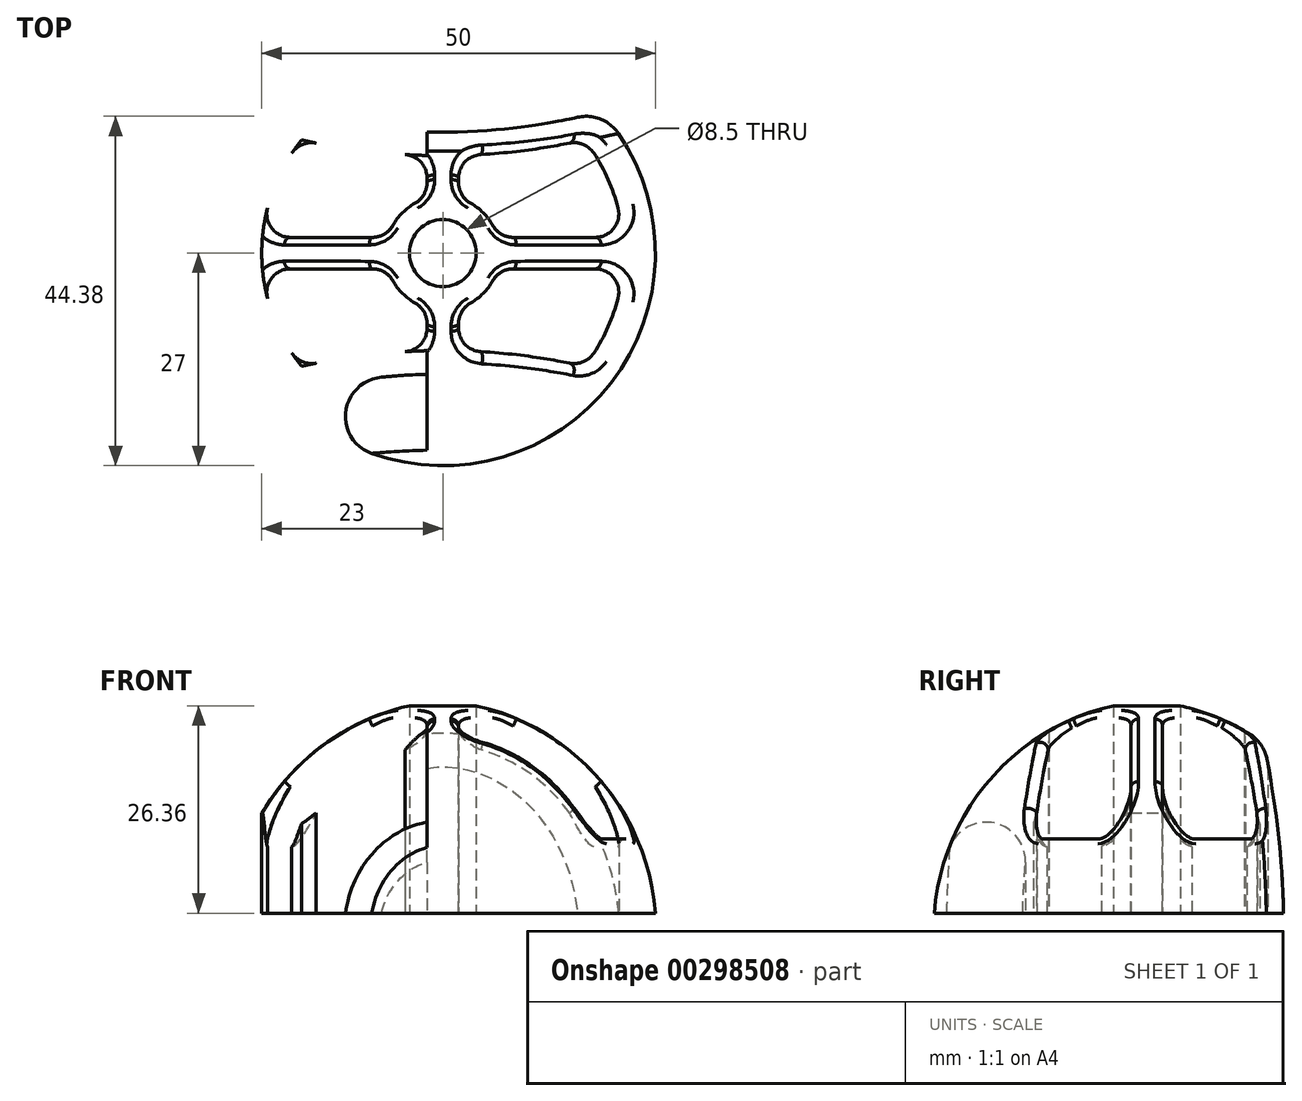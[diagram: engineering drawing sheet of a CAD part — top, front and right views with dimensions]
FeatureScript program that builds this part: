
annotation { "Feature Type Name" : "Feature", "Feature Type Description" : "" }
export const myFeature = defineFeature(function(context is Context, id is Id, definition is map)
    precondition{}
    {
        {
            var Q0;
            Q0=qCreatedBy(makeId("Top.planeOp"),FACE);
            var sketch = newSketch(context, id + "F0", { "sketchPlane" : qUnion([Q0])});
            skCircle(sketch, "E0", {"center": v(0, 0) * mm, "radius": 27 * mm});
            skSolve(sketch);
        }
        {
            var Q0;
            Q0=qCreatedBy(makeId("Right.planeOp"),FACE);
            var sketch = newSketch(context, id + "F1", { "sketchPlane" : qUnion([Q0])});
            skLineSegment(sketch, "E1", {"start": v(0, 0) * mm, "end": v(0, 27) * mm});
            skLineSegment(sketch, "E2", {"start": v(27, 0) * mm, "end": v(0, 0) * mm});
            skArc(sketch, "E3", {"start": v(27, 0) * mm, "mid": v(18.5, 18.5) * mm, "end": v(0, 27) * mm});
            skSolve(sketch);
        }
        {
            var Q0;
            Q0=makeQuery(id+"F1.imprint","IMPRINT",FACE,{"disambiguationData":[TD([[makeQuery(id+"F1.imprint","IMPRINT",EDGE,{"derivedFrom":sQuery(id+"F1.wireOp",EDGE,"E1")}),-1.0]])]});
            var Q1;
            Q1=sQuery(id+"F0.wireOp",EDGE,"E0");
            sweep(context, id + "F2", {"profiles" : qUnion([Q0]), "path" : qUnion([Q1])});
        }
        {
            var Q0;
            Q0=makeQuery(id+"F2.opSweep","SWEPT_FACE",FACE,{"disambiguationData":[OSD([sQuery(id+"F0.wireOp",EDGE,"E0"),sQuery(id+"F1.wireOp",EDGE,"E2")])]});
            var sketch = newSketch(context, id + "F3", { "sketchPlane" : qUnion([Q0])});
            skCircle(sketch, "E4", {"center": v(0, 0) * mm, "radius": 4.25 * mm});
            skArc(sketch, "E5.0", {"start": v(-17.95, -14.38) * mm, "mid": v(-23, 0) * mm, "end": v(-17.95, 14.38) * mm});
            skCircle(sketch, "E6.0", {"center": v(0, 0) * mm, "radius": 7.25 * mm});
            skLineSegment(sketch, "E7", {"start": v(0, 0) * mm, "end": v(-30.25, 0) * mm, "construction": true});
            skLineSegment(sketch, "E8", {"start": v(-6.97, -2) * mm, "end": v(-22.91, -2) * mm});
            skLineSegment(sketch, "E9", {"start": v(-6.97, 2) * mm, "end": v(-22.91, 2) * mm});
            skLineSegment(sketch, "E10.1.0", {"start": v(2, -6.97) * mm, "end": v(2, -15.4) * mm});
            skLineSegment(sketch, "E10.1.1", {"start": v(-2, -6.97) * mm, "end": v(-2, -15.4) * mm});
            skLineSegment(sketch, "E10.2.0", {"start": v(6.97, 2) * mm, "end": v(22.91, 2) * mm});
            skLineSegment(sketch, "E10.2.1", {"start": v(6.97, -2) * mm, "end": v(22.91, -2) * mm});
            skLineSegment(sketch, "E10.3.0", {"start": v(-2, 6.97) * mm, "end": v(-2, 15.4) * mm});
            skLineSegment(sketch, "E10.3.1", {"start": v(2, 6.97) * mm, "end": v(2, 15.4) * mm});
            skCircle(sketch, "E11.0", {"center": v(0, 0) * mm, "radius": 27 * mm});
            skArc(sketch, "E12", {"start": v(20.12, -18) * mm, "mid": v(0, -15.37) * mm, "end": v(-20.12, -18) * mm});
            skArc(sketch, "E13.MirrorCS", {"start": v(20.12, 18) * mm, "mid": v(0, 15.37) * mm, "end": v(-20.12, 18) * mm});
            skLineSegment(sketch, "E14", {"start": v(-20.12, -18) * mm, "end": v(20.12, -18) * mm, "construction": true});
            skArc(sketch, "E15.0", {"start": v(17.95, -14.38) * mm, "mid": v(0, -12.37) * mm, "end": v(-17.95, -14.38) * mm});
            skArc(sketch, "E16.MirrorCS", {"start": v(17.95, 14.38) * mm, "mid": v(0, 12.37) * mm, "end": v(-17.95, 14.38) * mm});
            skArc(sketch, "E17.trimOffspring", {"start": v(17.95, 14.38) * mm, "mid": v(23, 0) * mm, "end": v(17.95, -14.38) * mm});
            skPoint(sketch, "E18.orphan", {"position": v(-22.15, 15.44) * mm});
            skPoint(sketch, "E19.orphan", {"position": v(-22.15, -15.44) * mm});
            skPoint(sketch, "E20.orphan", {"position": v(22.15, -15.44) * mm});
            skPoint(sketch, "E21.orphan", {"position": v(22.15, 15.44) * mm});
            skLineSegment(sketch, "E22", {"start": v(-20.12, 18) * mm, "end": v(20.12, 18) * mm, "construction": true});
            skSolve(sketch);
        }
        {
            var Q0;
            {var subQ0=sQuery(id+"F3.wireOp",EDGE,"E8");Q0=makeQuery(id+"F3.imprint","IMPRINT",FACE,{"disambiguationData":[TD([[makeQuery(id+"F3.imprint","IMPRINT",EDGE,{"derivedFrom":subQ0}),1.0]])]});}
            var Q1;
            {var subQ0=sQuery(id+"F3.wireOp",EDGE,"E9");Q1=makeQuery(id+"F3.imprint","IMPRINT",FACE,{"disambiguationData":[TD([[makeQuery(id+"F3.imprint","IMPRINT",EDGE,{"derivedFrom":subQ0}),-1.0]])]});}
            var Q2;
            {var subQ0=sQuery(id+"F3.wireOp",EDGE,"E10.2.0");Q2=makeQuery(id+"F3.imprint","IMPRINT",FACE,{"disambiguationData":[TD([[makeQuery(id+"F3.imprint","IMPRINT",EDGE,{"derivedFrom":subQ0}),1.0]])]});}
            var Q3;
            {var subQ0=sQuery(id+"F3.wireOp",EDGE,"E10.1.0");Q3=makeQuery(id+"F3.imprint","IMPRINT",FACE,{"disambiguationData":[TD([[makeQuery(id+"F3.imprint","IMPRINT",EDGE,{"derivedFrom":subQ0}),1.0]])]});}
            var Q4;
            Q4=makeQuery(id+"F3.imprint","IMPRINT",FACE,{"disambiguationData":[TD([[makeQuery(id+"F3.imprint","IMPRINT",EDGE,{"derivedFrom":sQuery(id+"F3.wireOp",EDGE,"E4")}),1.0]])]});
            extrude(context, id + "F4", {"entities" : qUnion([Q0, Q1, Q2, Q3, Q4]), "operationType" : NewBodyOperationType.REMOVE, "endBound" : BoundingType.THROUGH_ALL, "oppositeDirection" : true, "depth" : 25 * mm});
        }
        {
            var Q0;
            Q0=makeQuery(id+"F4.boolean.opBoolean","COPY",EDGE,{"derivedFrom":makeQuery(id+"F4.opExtrude","SWEPT_EDGE",EDGE,{"disambiguationData":[OSD([sQuery(id+"F3.wireOp",EDGE,"E6.0"),sQuery(id+"F3.wireOp",EDGE,"E10.1.1")])]})});
            var Q1;
            Q1=makeQuery(id+"F4.boolean.opBoolean","COPY",EDGE,{"derivedFrom":makeQuery(id+"F4.opExtrude","SWEPT_EDGE",EDGE,{"disambiguationData":[OSD([sQuery(id+"F3.wireOp",EDGE,"E6.0"),sQuery(id+"F3.wireOp",EDGE,"E8")])]})});
            var Q2;
            Q2=makeQuery(id+"F4.boolean.opBoolean","COPY",EDGE,{"derivedFrom":makeQuery(id+"F4.opExtrude","SWEPT_EDGE",EDGE,{"disambiguationData":[OSD([sQuery(id+"F3.wireOp",EDGE,"E6.0"),sQuery(id+"F3.wireOp",EDGE,"E10.3.0")])]})});
            var Q3;
            Q3=makeQuery(id+"F4.boolean.opBoolean","COPY",EDGE,{"derivedFrom":makeQuery(id+"F4.opExtrude","SWEPT_EDGE",EDGE,{"disambiguationData":[OSD([sQuery(id+"F3.wireOp",EDGE,"E6.0"),sQuery(id+"F3.wireOp",EDGE,"E9")])]})});
            var Q4;
            Q4=makeQuery(id+"F4.boolean.opBoolean","COPY",EDGE,{"derivedFrom":makeQuery(id+"F4.opExtrude","SWEPT_EDGE",EDGE,{"disambiguationData":[OSD([sQuery(id+"F3.wireOp",EDGE,"E6.0"),sQuery(id+"F3.wireOp",EDGE,"E10.3.1")])]})});
            var Q5;
            Q5=makeQuery(id+"F4.boolean.opBoolean","COPY",EDGE,{"derivedFrom":makeQuery(id+"F4.opExtrude","SWEPT_EDGE",EDGE,{"disambiguationData":[OSD([sQuery(id+"F3.wireOp",EDGE,"E6.0"),sQuery(id+"F3.wireOp",EDGE,"E10.2.0")])]})});
            var Q6;
            Q6=makeQuery(id+"F4.boolean.opBoolean","COPY",EDGE,{"derivedFrom":makeQuery(id+"F4.opExtrude","SWEPT_EDGE",EDGE,{"disambiguationData":[OSD([sQuery(id+"F3.wireOp",EDGE,"E6.0"),sQuery(id+"F3.wireOp",EDGE,"E10.2.1")])]})});
            var Q7;
            Q7=makeQuery(id+"F4.boolean.opBoolean","COPY",EDGE,{"derivedFrom":makeQuery(id+"F4.opExtrude","SWEPT_EDGE",EDGE,{"disambiguationData":[OSD([sQuery(id+"F3.wireOp",EDGE,"E6.0"),sQuery(id+"F3.wireOp",EDGE,"E10.1.0")])]})});
            var Q8;
            Q8=makeQuery(id+"F4.boolean.opBoolean","COPY",EDGE,{"derivedFrom":makeQuery(id+"F4.opExtrude","SWEPT_EDGE",EDGE,{"disambiguationData":[OSD([sQuery(id+"F3.wireOp",EDGE,"E5.0"),sQuery(id+"F3.wireOp",EDGE,"E10.1.1")])]})});
            var Q9;
            Q9=makeQuery(id+"F4.boolean.opBoolean","COPY",EDGE,{"derivedFrom":makeQuery(id+"F4.opExtrude","SWEPT_EDGE",EDGE,{"disambiguationData":[OSD([sQuery(id+"F3.wireOp",EDGE,"E5.0"),sQuery(id+"F3.wireOp",EDGE,"E8")])]})});
            var Q10;
            Q10=makeQuery(id+"F4.boolean.opBoolean","COPY",EDGE,{"derivedFrom":makeQuery(id+"F4.opExtrude","SWEPT_EDGE",EDGE,{"disambiguationData":[OSD([sQuery(id+"F3.wireOp",EDGE,"E5.0"),sQuery(id+"F3.wireOp",EDGE,"E9")])]})});
            var Q11;
            Q11=makeQuery(id+"F4.boolean.opBoolean","COPY",EDGE,{"derivedFrom":makeQuery(id+"F4.opExtrude","SWEPT_EDGE",EDGE,{"disambiguationData":[OSD([sQuery(id+"F3.wireOp",EDGE,"E5.0"),sQuery(id+"F3.wireOp",EDGE,"E10.3.0")])]})});
            var Q12;
            Q12=makeQuery(id+"F4.boolean.opBoolean","COPY",EDGE,{"derivedFrom":makeQuery(id+"F4.opExtrude","SWEPT_EDGE",EDGE,{"disambiguationData":[OSD([sQuery(id+"F3.wireOp",EDGE,"E5.0"),sQuery(id+"F3.wireOp",EDGE,"E10.3.1")])]})});
            var Q13;
            Q13=makeQuery(id+"F4.boolean.opBoolean","COPY",EDGE,{"derivedFrom":makeQuery(id+"F4.opExtrude","SWEPT_EDGE",EDGE,{"disambiguationData":[OSD([sQuery(id+"F3.wireOp",EDGE,"E5.0"),sQuery(id+"F3.wireOp",EDGE,"E10.2.0")])]})});
            var Q14;
            Q14=makeQuery(id+"F4.boolean.opBoolean","COPY",EDGE,{"derivedFrom":makeQuery(id+"F4.opExtrude","SWEPT_EDGE",EDGE,{"disambiguationData":[OSD([sQuery(id+"F3.wireOp",EDGE,"E5.0"),sQuery(id+"F3.wireOp",EDGE,"E10.2.1")])]})});
            var Q15;
            Q15=makeQuery(id+"F4.boolean.opBoolean","COPY",EDGE,{"derivedFrom":makeQuery(id+"F4.opExtrude","SWEPT_EDGE",EDGE,{"disambiguationData":[OSD([sQuery(id+"F3.wireOp",EDGE,"E5.0"),sQuery(id+"F3.wireOp",EDGE,"E10.1.0")])]})});
            var Q16;
            Q16=makeQuery(id+"F4.boolean.opBoolean","COPY",EDGE,{"derivedFrom":makeQuery(id+"F4.opExtrude","SWEPT_EDGE",EDGE,{"disambiguationData":[OSD([sQuery(id+"F3.wireOp",EDGE,"E16.MirrorCS"),sQuery(id+"F3.wireOp",EDGE,"E17.trimOffspring")])]})});
            var Q17;
            Q17=makeQuery(id+"F4.boolean.opBoolean","COPY",EDGE,{"derivedFrom":makeQuery(id+"F4.opExtrude","SWEPT_EDGE",EDGE,{"disambiguationData":[OSD([sQuery(id+"F3.wireOp",EDGE,"E15.0"),sQuery(id+"F3.wireOp",EDGE,"E17.trimOffspring")])]})});
            fillet(context, id + "F5", {"entities" : qUnion([Q0, Q1, Q2, Q3, Q4, Q5, Q6, Q7, Q8, Q9, Q10, Q11, Q12, Q13, Q14, Q15, Q16, Q17]), "radius" : 3 * mm, "tangentPropagation" : true, "allowEdgeOverflow" : false});
        }
        {
            var Q0;
            Q0=makeQuery(id+"F5.opFillet","BLEND_EDGE",EDGE,{"blendedFrom":[makeQuery(id+"F4.boolean.opBoolean","COPY",EDGE,{"derivedFrom":makeQuery(id+"F4.opExtrude","SWEPT_EDGE",EDGE,{"disambiguationData":[OSD([sQuery(id+"F3.wireOp",EDGE,"E6.0"),sQuery(id+"F3.wireOp",EDGE,"E10.3.1")])]})}),makeQuery(id+"F2.opSweep","SWEPT_FACE",FACE,{"disambiguationData":[OSD([sQuery(id+"F0.wireOp",EDGE,"E0"),sQuery(id+"F1.wireOp",EDGE,"E3")])]})],"blendedInto":[makeQuery(id+"F2.opSweep","SWEPT_FACE",FACE,{"disambiguationData":[OSD([sQuery(id+"F0.wireOp",EDGE,"E0"),sQuery(id+"F1.wireOp",EDGE,"E3")])]})]});
            var Q1;
            Q1=makeQuery(id+"F5.opFillet","BLEND_EDGE",EDGE,{"blendedFrom":[makeQuery(id+"F4.boolean.opBoolean","COPY",EDGE,{"derivedFrom":makeQuery(id+"F4.opExtrude","SWEPT_EDGE",EDGE,{"disambiguationData":[OSD([sQuery(id+"F3.wireOp",EDGE,"E6.0"),sQuery(id+"F3.wireOp",EDGE,"E10.1.1")])]})}),makeQuery(id+"F2.opSweep","SWEPT_FACE",FACE,{"disambiguationData":[OSD([sQuery(id+"F0.wireOp",EDGE,"E0"),sQuery(id+"F1.wireOp",EDGE,"E3")])]})],"blendedInto":[makeQuery(id+"F2.opSweep","SWEPT_FACE",FACE,{"disambiguationData":[OSD([sQuery(id+"F0.wireOp",EDGE,"E0"),sQuery(id+"F1.wireOp",EDGE,"E3")])]})]});
            var Q2;
            Q2=makeQuery(id+"F5.opFillet","BLEND_EDGE",EDGE,{"blendedFrom":[makeQuery(id+"F4.boolean.opBoolean","COPY",EDGE,{"derivedFrom":makeQuery(id+"F4.opExtrude","SWEPT_EDGE",EDGE,{"disambiguationData":[OSD([sQuery(id+"F3.wireOp",EDGE,"E6.0"),sQuery(id+"F3.wireOp",EDGE,"E10.3.0")])]})}),makeQuery(id+"F2.opSweep","SWEPT_FACE",FACE,{"disambiguationData":[OSD([sQuery(id+"F0.wireOp",EDGE,"E0"),sQuery(id+"F1.wireOp",EDGE,"E3")])]})],"blendedInto":[makeQuery(id+"F2.opSweep","SWEPT_FACE",FACE,{"disambiguationData":[OSD([sQuery(id+"F0.wireOp",EDGE,"E0"),sQuery(id+"F1.wireOp",EDGE,"E3")])]})]});
            var Q3;
            Q3=makeQuery(id+"F5.opFillet","BLEND_EDGE",EDGE,{"blendedFrom":[makeQuery(id+"F4.boolean.opBoolean","COPY",EDGE,{"derivedFrom":makeQuery(id+"F4.opExtrude","SWEPT_EDGE",EDGE,{"disambiguationData":[OSD([sQuery(id+"F3.wireOp",EDGE,"E6.0"),sQuery(id+"F3.wireOp",EDGE,"E10.2.1")])]})}),makeQuery(id+"F2.opSweep","SWEPT_FACE",FACE,{"disambiguationData":[OSD([sQuery(id+"F0.wireOp",EDGE,"E0"),sQuery(id+"F1.wireOp",EDGE,"E3")])]})],"blendedInto":[makeQuery(id+"F2.opSweep","SWEPT_FACE",FACE,{"disambiguationData":[OSD([sQuery(id+"F0.wireOp",EDGE,"E0"),sQuery(id+"F1.wireOp",EDGE,"E3")])]})]});
            var Q4;
            Q4=makeQuery(id+"F4.boolean.opBoolean","COPY",EDGE,{"derivedFrom":makeQuery(id+"F4.opExtrude","CAP_EDGE",EDGE,{"disambiguationData":[OSD([sQuery(id+"F3.wireOp",EDGE,"E4")])],"isStart":true})});
            fillet(context, id + "F6", {"entities" : qUnion([Q0, Q1, Q2, Q3, Q4]), "radius" : 1 * mm, "tangentPropagation" : true, "allowEdgeOverflow" : false});
        }
        {
            var Q0;
            {var subQ0=sQuery(id+"F3.wireOp",EDGE,"E12");var subQ1=sQuery(id+"F3.wireOp",EDGE,"E11.0");var subQ2=makeQuery(id+"F3.imprint","INTERSECT",VERTEX,{"disambiguationData":[OD(0.0)],"derivedFrom":[subQ1,subQ0]});Q0=makeQuery(id+"F3.imprint","IMPRINT",FACE,{"disambiguationData":[TD([[makeQuery(id+"F3.imprint","IMPRINT",EDGE,{"disambiguationData":[TD([[subQ2,-1.0]])],"derivedFrom":subQ1}),-1.0]])]});}
            var Q1;
            {var subQ0=sQuery(id+"F3.wireOp",EDGE,"E13.MirrorCS");var subQ1=sQuery(id+"F3.wireOp",EDGE,"E11.0");var subQ2=makeQuery(id+"F3.imprint","INTERSECT",VERTEX,{"disambiguationData":[OD(0.0)],"derivedFrom":[subQ1,subQ0]});Q1=makeQuery(id+"F3.imprint","IMPRINT",FACE,{"disambiguationData":[TD([[makeQuery(id+"F3.imprint","IMPRINT",EDGE,{"disambiguationData":[TD([[subQ2,1.0]])],"derivedFrom":subQ1}),-1.0]])]});}
            extrude(context, id + "F7", {"entities" : qUnion([Q0, Q1]), "operationType" : NewBodyOperationType.REMOVE, "oppositeDirection" : true, "depth" : 25 * mm});
        }
        {
            var Q0;
            Q0=makeQuery(id+"F7.boolean.opBoolean","INTERSECT",EDGE,{"derivedFrom":[makeQuery(id+"F2.opSweep","SWEPT_FACE",FACE,{"disambiguationData":[OSD([sQuery(id+"F0.wireOp",EDGE,"E0"),sQuery(id+"F1.wireOp",EDGE,"E3")])]}),makeQuery(id+"F7.opExtrude","SWEPT_FACE",FACE,{"disambiguationData":[OSD([sQuery(id+"F3.wireOp",EDGE,"E12")])]})]});
            var Q1;
            Q1=makeQuery(id+"F7.boolean.opBoolean","INTERSECT",EDGE,{"derivedFrom":[makeQuery(id+"F2.opSweep","SWEPT_FACE",FACE,{"disambiguationData":[OSD([sQuery(id+"F0.wireOp",EDGE,"E0"),sQuery(id+"F1.wireOp",EDGE,"E3")])]}),makeQuery(id+"F7.opExtrude","SWEPT_FACE",FACE,{"disambiguationData":[OSD([sQuery(id+"F3.wireOp",EDGE,"E13.MirrorCS")])]})]});
            fillet(context, id + "F8", {"entities" : qUnion([Q0, Q1]), "radius" : 5 * mm, "tangentPropagation" : true, "allowEdgeOverflow" : false});
        }
    });
